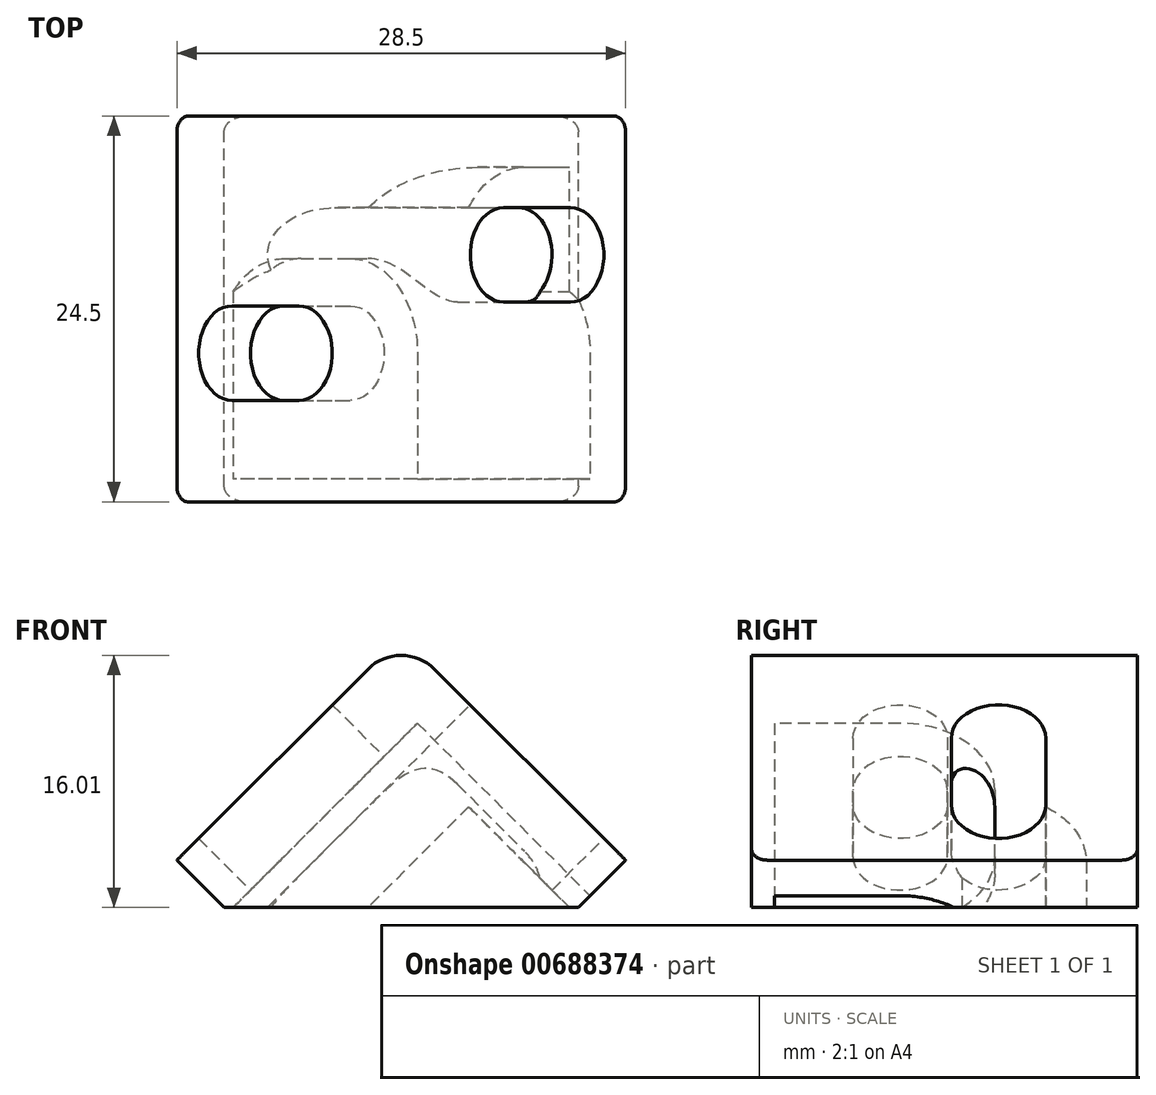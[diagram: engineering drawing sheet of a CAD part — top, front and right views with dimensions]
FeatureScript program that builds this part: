
annotation { "Feature Type Name" : "Feature", "Feature Type Description" : "" }
export const myFeature = defineFeature(function(context is Context, id is Id, definition is map)
    precondition{}
    {
        {
            var Q0;
            Q0=qCreatedBy(makeId("Front.planeOp"),FACE);
            var sketch = newSketch(context, id + "F0", { "sketchPlane" : qUnion([Q0])});
            skLineSegment(sketch, "E0", {"start": v(0, 0) * mm, "end": v(-11.25, 0) * mm});
            skLineSegment(sketch, "E1", {"start": v(-14.25, 3) * mm, "end": v(0, 17.25) * mm});
            skLineSegment(sketch, "E2", {"start": v(0, 17.25) * mm, "end": v(14.25, 3) * mm});
            skLineSegment(sketch, "E3", {"start": v(11.25, 0) * mm, "end": v(0, 0) * mm});
            skLineSegment(sketch, "E4", {"start": v(-14.25, 3) * mm, "end": v(-11.25, 0) * mm});
            skLineSegment(sketch, "E5", {"start": v(14.25, 3) * mm, "end": v(11.25, 0) * mm});
            skPoint(sketch, "E6.start.orphan", {"position": v(-14.25, 0) * mm});
            skPoint(sketch, "E7.end.orphan", {"position": v(14.25, 0) * mm});
            skSolve(sketch);
        }
        {
            var Q0;
            Q0 = qSketchRegion(id + "F0", true);
            extrude(context, id + "F1", {"entities" : qUnion([Q0]), "endBound" : BoundingType.SYMMETRIC, "depth" : 24.5 * mm, "offsetDistance" : 25 * mm});
        }
        {
            var Q0;
            Q0=makeQuery(id+"F1.opExtrude","SWEPT_EDGE",EDGE,{"disambiguationData":[OSD([sQuery(id+"F0.wireOp",EDGE,"E1"),sQuery(id+"F0.wireOp",EDGE,"E2")])]});
            fillet(context, id + "F2", {"entities" : qUnion([Q0]), "radius" : 3 * mm, "tangentPropagation" : true, "allowEdgeOverflow" : false});
        }
        {
            var Q0;
            Q0=makeQuery(id+"F1.opExtrude","SWEPT_FACE",FACE,{"disambiguationData":[OSD([sQuery(id+"F0.wireOp",EDGE,"E2")])]});
            var sketch = newSketch(context, id + "F3", { "sketchPlane" : qUnion([Q0])});
            skArc(sketch, "E8", {"start": v(6.43, 3) * mm, "mid": v(3.43, 6) * mm, "end": v(0.43, 3) * mm});
            skArc(sketch, "E9", {"start": v(0.43, -3) * mm, "mid": v(3.43, -6) * mm, "end": v(6.43, -3) * mm});
            skLineSegment(sketch, "E10", {"start": v(6.43, 3) * mm, "end": v(6.43, -3) * mm});
            skLineSegment(sketch, "E11", {"start": v(0.43, 3) * mm, "end": v(0.43, -3) * mm});
            skSolve(sketch);
        }
        {
            var Q0;
            Q0 = qSketchRegion(id + "F3", true);
            extrude(context, id + "F4", {"entities" : qUnion([Q0]), "operationType" : NewBodyOperationType.REMOVE, "endBound" : BoundingType.THROUGH_ALL, "oppositeDirection" : true, "depth" : 25 * mm, "offsetDistance" : 25 * mm});
        }
        {
            var Q0;
            Q0 = qBodyType(qCreatedBy(id + "F6" ,EDGE), BodyType.WIRE);
            var Q1;
            Q1=makeQuery(id+"F1.opExtrude","SWEPT_FACE",FACE,{"disambiguationData":[OSD([sQuery(id+"F0.wireOp",EDGE,"E4")])]});
            cPlane(context, id + "F5", {"entities" : qUnion([Q0, Q1]), "cplaneType" : CPlaneType.OFFSET, "offset" : 4 * mm, "oppositeDirection" : true, "width" : 150 * mm, "height" : 150 * mm});
        }
        {
            var Q0;
            Q0=qCreatedBy(id+"F5.planeOp",FACE);
            var sketch = newSketch(context, id + "F6", { "sketchPlane" : qUnion([Q0])});
            skLineSegment(sketch, "E12", {"start": v(7.95, -7.95) * mm, "end": v(7.95, -7.95) * mm});
            skPoint(sketch, "E13.center.orphan", {"position": v(2.9, -1.95) * mm});
            skPoint(sketch, "E13.start.orphan", {"position": v(-3.1, -1.95) * mm});
            skPoint(sketch, "E14.center.orphan", {"position": v(-3, -3.43) * mm});
            skPoint(sketch, "E14.end.orphan", {"position": v(-7.25, -3.43) * mm});
            skPoint(sketch, "E14.start.orphan", {"position": v(-3, -7.95) * mm});
            skPoint(sketch, "E15.start.orphan", {"position": v(2.9, -7.95) * mm});
            skArc(sketch, "E16", {"start": v(-3, 2.57) * mm, "mid": v(-7.24, 0.81) * mm, "end": v(-9, -3.43) * mm});
            skArc(sketch, "E17", {"start": v(9, -3.43) * mm, "mid": v(7.2, 0.85) * mm, "end": v(2.9, 2.57) * mm});
            skLineSegment(sketch, "E18", {"start": v(-3, 2.57) * mm, "end": v(-3, 2.57) * mm});
            skLineSegment(sketch, "E19", {"start": v(-9, -3.43) * mm, "end": v(-9, -10.68) * mm});
            skLineSegment(sketch, "E20", {"start": v(9, -3.43) * mm, "end": v(9, -10.68) * mm});
            skLineSegment(sketch, "E21", {"start": v(9, -10.68) * mm, "end": v(-9, -10.68) * mm});
            skLineSegment(sketch, "E22", {"start": v(2.9, 2.57) * mm, "end": v(-3, 2.57) * mm});
            skSolve(sketch);
        }
        {
            var Q0;
            Q0 = qSketchRegion(id + "F6", true);
            extrude(context, id + "F7", {"entities" : qUnion([Q0]), "operationType" : NewBodyOperationType.REMOVE, "oppositeDirection" : true, "depth" : 11.5 * mm, "offsetDistance" : 25 * mm});
        }
        {
            var Q0;
            Q0=makeQuery(id+"F1.opExtrude","SWEPT_FACE",FACE,{"disambiguationData":[OSD([sQuery(id+"F0.wireOp",EDGE,"E5")])]});
            var sketch = newSketch(context, id + "F8", { "sketchPlane" : qUnion([Q0])});
            skArc(sketch, "E23", {"start": v(0.2, 3) * mm, "mid": v(-2.8, 6) * mm, "end": v(-5.8, 3) * mm});
            skArc(sketch, "E24", {"start": v(-5.8, -3) * mm, "mid": v(-2.8, -6) * mm, "end": v(0.2, -3) * mm});
            skLineSegment(sketch, "E25", {"start": v(0.2, -3) * mm, "end": v(0.2, 3) * mm});
            skLineSegment(sketch, "E26", {"start": v(-5.8, -3) * mm, "end": v(-5.8, 3) * mm});
            skArc(sketch, "E27", {"start": v(-2.8, -9) * mm, "mid": v(1.44, -7.24) * mm, "end": v(3.2, -3) * mm});
            skArc(sketch, "E28", {"start": v(3.2, 3) * mm, "mid": v(1.44, 7.24) * mm, "end": v(-2.8, 9) * mm});
            skLineSegment(sketch, "E29", {"start": v(-2.8, -3) * mm, "end": v(3.2, -3) * mm});
            skLineSegment(sketch, "E30", {"start": v(3.2, -3) * mm, "end": v(3.2, 3) * mm});
            skLineSegment(sketch, "E31", {"start": v(-2.8, 9) * mm, "end": v(-10.8, 9) * mm});
            skLineSegment(sketch, "E32", {"start": v(-10.8, 9) * mm, "end": v(-10.8, -9) * mm});
            skPoint(sketch, "E32.endSnap0", {"position": v(-2.8, -9) * mm});
            skLineSegment(sketch, "E33", {"start": v(-10.8, -9) * mm, "end": v(-2.8, -9) * mm});
            skSolve(sketch);
        }
        {
            var Q0;
            Q0=makeQuery(id+"F8.imprint","IMPRINT",FACE,{"disambiguationData":[TD([[makeQuery(id+"F8.imprint","IMPRINT",EDGE,{"derivedFrom":sQuery(id+"F8.wireOp",EDGE,"E23")}),1.0]])]});
            extrude(context, id + "F9", {"entities" : qUnion([Q0]), "operationType" : NewBodyOperationType.REMOVE, "endBound" : BoundingType.THROUGH_ALL, "oppositeDirection" : true, "depth" : 25 * mm, "offsetDistance" : 25 * mm});
        }
        {
            var Q0;
            Q0 = qSketchRegion(id + "F8", true);
            extrude(context, id + "F10", {"entities" : qUnion([Q0]), "operationType" : NewBodyOperationType.REMOVE, "oppositeDirection" : true, "depth" : 15.5 * mm, "offsetDistance" : 25 * mm});
        }
        {
            var Q0;
            Q0=makeQuery(id+"F1.opExtrude","CAP_EDGE",EDGE,{"disambiguationData":[OSD([sQuery(id+"F0.wireOp",EDGE,"E5")])],"isStart":true});
            var Q1;
            Q1=makeQuery(id+"F1.opExtrude","CAP_EDGE",EDGE,{"disambiguationData":[OSD([sQuery(id+"F0.wireOp",EDGE,"E4")])],"isStart":true});
            var Q2;
            Q2=makeQuery(id+"F1.opExtrude","CAP_EDGE",EDGE,{"disambiguationData":[OSD([sQuery(id+"F0.wireOp",EDGE,"E4")])],"isStart":false});
            var Q3;
            Q3=makeQuery(id+"F1.opExtrude","CAP_EDGE",EDGE,{"disambiguationData":[OSD([sQuery(id+"F0.wireOp",EDGE,"E5")])],"isStart":false});
            fillet(context, id + "F11", {"entities" : qUnion([Q0, Q1, Q2, Q3]), "radius" : 1 * mm, "tangentPropagation" : true, "allowEdgeOverflow" : false});
        }
    });
